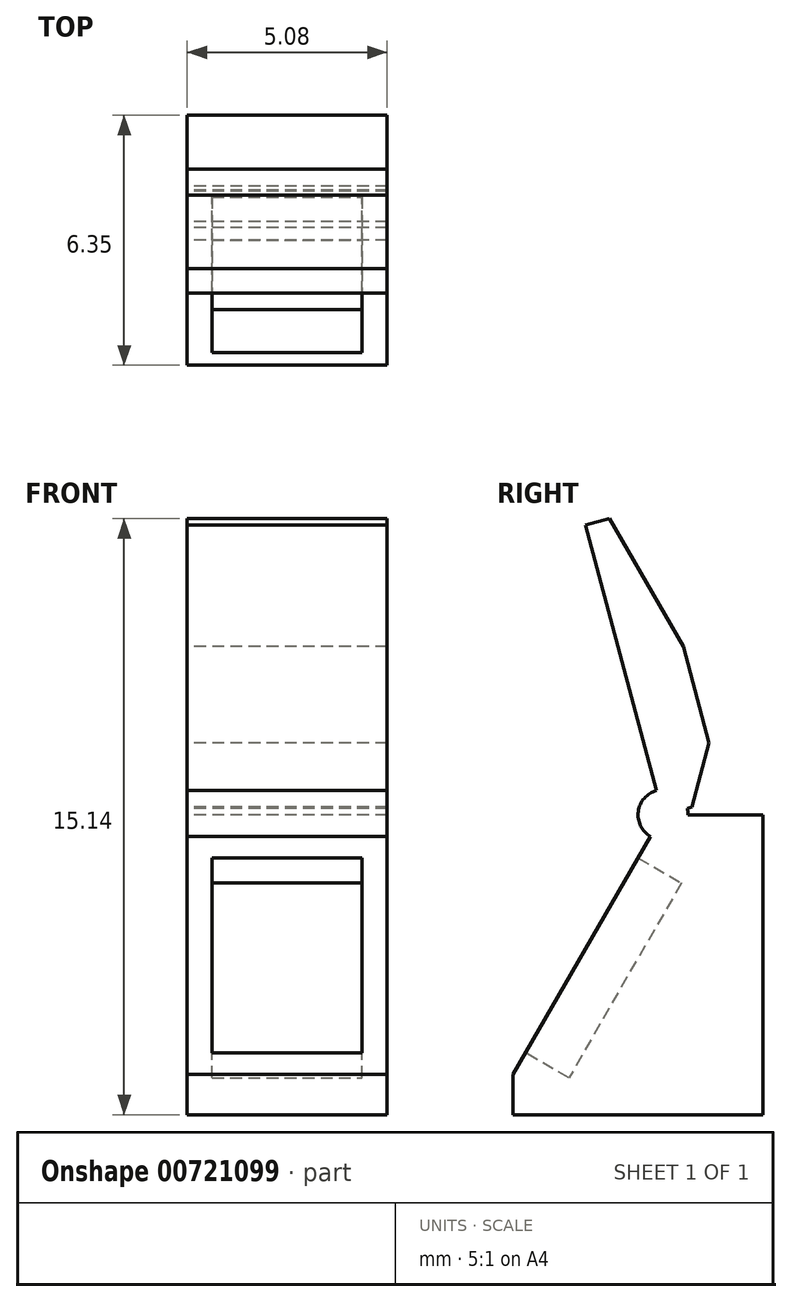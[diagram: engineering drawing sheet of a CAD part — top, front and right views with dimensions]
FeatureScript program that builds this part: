
annotation { "Feature Type Name" : "Feature", "Feature Type Description" : "" }
export const myFeature = defineFeature(function(context is Context, id is Id, definition is map)
    precondition{}
    {
        {
            var Q0;
            Q0=qCreatedBy(makeId("Right.planeOp"),FACE);
            var sketch = newSketch(context, id + "F0", { "sketchPlane" : qUnion([Q0])});
            skLineSegment(sketch, "E0", {"start": v(-6.35, 0) * mm, "end": v(-6.35, 1.02) * mm});
            skLineSegment(sketch, "E1", {"start": v(-6.35, 1.02) * mm, "end": v(-2.54, 7.62) * mm});
            skLineSegment(sketch, "E2", {"start": v(-2.54, 7.62) * mm, "end": v(0, 7.62) * mm});
            skLineSegment(sketch, "E3", {"start": v(0, 7.62) * mm, "end": v(0, 0) * mm});
            skLineSegment(sketch, "E4", {"start": v(0, 0) * mm, "end": v(-6.35, 0) * mm});
            skSolve(sketch);
        }
        {
            var Q0;
            Q0 = qSketchRegion(id + "F0", true);
            extrude(context, id + "F1", {"entities" : qUnion([Q0]), "endBound" : BoundingType.SYMMETRIC, "depth" : 5.08 * mm, "offsetDistance" : 25.4 * mm});
        }
        {
            var Q0;
            Q0=qCreatedBy(makeId("Right.planeOp"),FACE);
            var sketch = newSketch(context, id + "F2", { "sketchPlane" : qUnion([Q0])});
            skLineSegment(sketch, "E5", {"start": v(-2.7, 8.23) * mm, "end": v(-4.51, 14.98) * mm});
            skLineSegment(sketch, "E6", {"start": v(-4.51, 14.98) * mm, "end": v(-3.9, 15.14) * mm});
            skLineSegment(sketch, "E7", {"start": v(-3.9, 15.14) * mm, "end": v(-2.03, 11.9) * mm});
            skLineSegment(sketch, "E8", {"start": v(-2.03, 11.9) * mm, "end": v(-1.37, 9.45) * mm});
            skLineSegment(sketch, "E9", {"start": v(-1.93, 7.78) * mm, "end": v(-1.8, 7.82) * mm});
            skLineSegment(sketch, "E10", {"start": v(-1.8, 7.82) * mm, "end": v(-1.37, 9.45) * mm});
            skArc(sketch, "E11", {"start": v(-2.7, 8.23) * mm, "mid": v(-2.86, 7.07) * mm, "end": v(-1.93, 7.78) * mm});
            skLineSegment(sketch, "E12", {"start": v(-2.54, 7.62) * mm, "end": v(-1.93, 7.78) * mm, "construction": true});
            skLineSegment(sketch, "E13", {"start": v(-2.54, 7.62) * mm, "end": v(-2.7, 8.23) * mm, "construction": true});
            skSolve(sketch);
        }
        {
            var Q0;
            Q0=makeQuery(id+"F2.imprint","IMPRINT",FACE,{"disambiguationData":[TD([[makeQuery(id+"F2.imprint","IMPRINT",EDGE,{"derivedFrom":sQuery(id+"F2.wireOp",EDGE,"E5")}),-1.0]])]});
            extrude(context, id + "F3", {"entities" : qUnion([Q0]), "operationType" : NewBodyOperationType.ADD, "endBound" : BoundingType.SYMMETRIC, "depth" : 5.08 * mm, "offsetDistance" : 25.4 * mm});
        }
        {
            var Q0;
            Q0=qCreatedBy(makeId("Right.planeOp"),FACE);
            var sketch = newSketch(context, id + "F4", { "sketchPlane" : qUnion([Q0])});
            skLineSegment(sketch, "E14", {"start": v(-6.6, 1.9) * mm, "end": v(-3.73, 6.84) * mm});
            skLineSegment(sketch, "E15", {"start": v(-3.73, 6.84) * mm, "end": v(-2.08, 5.89) * mm});
            skLineSegment(sketch, "E16", {"start": v(-2.08, 5.89) * mm, "end": v(-4.93, 0.94) * mm});
            skLineSegment(sketch, "E17", {"start": v(-4.93, 0.94) * mm, "end": v(-6.6, 1.9) * mm});
            skSolve(sketch);
        }
        {
            var Q0;
            {var subQ0=sQuery(id+"F4.wireOp",EDGE,"E15");Q0=makeQuery(id+"F4.imprint","IMPRINT",FACE,{"disambiguationData":[TD([[makeQuery(id+"F4.imprint","IMPRINT",EDGE,{"derivedFrom":subQ0}),-1.0]])]});}
            extrude(context, id + "F5", {"entities" : qUnion([Q0]), "operationType" : NewBodyOperationType.REMOVE, "endBound" : BoundingType.SYMMETRIC, "oppositeDirection" : true, "depth" : 3.8 * mm, "offsetDistance" : 25.4 * mm});
        }
    });
